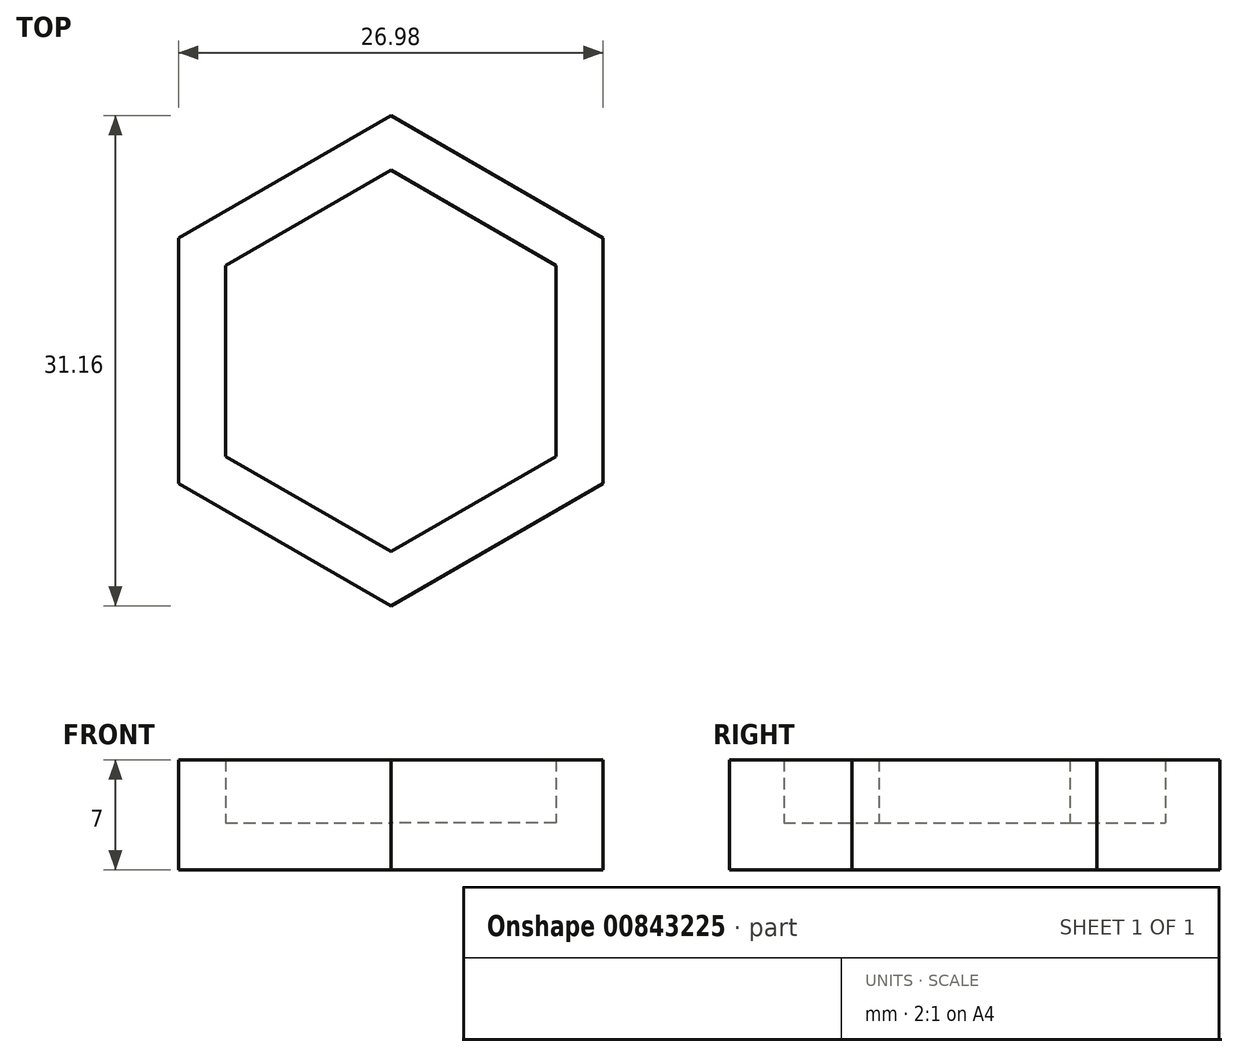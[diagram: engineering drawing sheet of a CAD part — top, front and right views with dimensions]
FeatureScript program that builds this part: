
annotation { "Feature Type Name" : "Feature", "Feature Type Description" : "" }
export const myFeature = defineFeature(function(context is Context, id is Id, definition is map)
    precondition{}
    {
        {
            var Q0;
            Q0=qCreatedBy(makeId("Top.planeOp"),FACE);
            var sketch = newSketch(context, id + "F0", { "sketchPlane" : qUnion([Q0])});
            skCircle(sketch, "E0.cCircle", {"center": v(0, 0) * mm, "radius": 10.49 * mm, "construction": true});
            skLineSegment(sketch, "E0.0", {"start": v(10.49, 6.06) * mm, "end": v(10.49, -6.06) * mm});
            skLineSegment(sketch, "E0.1", {"start": v(10.49, -6.06) * mm, "end": v(0, -12.11) * mm});
            skLineSegment(sketch, "E0.2", {"start": v(0, -12.11) * mm, "end": v(-10.49, -6.06) * mm});
            skLineSegment(sketch, "E0.3", {"start": v(-10.49, -6.06) * mm, "end": v(-10.5, 6.06) * mm});
            skLineSegment(sketch, "E0.4", {"start": v(-10.5, 6.06) * mm, "end": v(0, 12.11) * mm});
            skLineSegment(sketch, "E0.5", {"start": v(0, 12.11) * mm, "end": v(10.49, 6.06) * mm});
            skPoint(sketch, "E0.0.midPoint", {"position": v(10.49, 0) * mm});
            skLineSegment(sketch, "E1.0", {"start": v(-13.49, -7.79) * mm, "end": v(-13.49, 7.79) * mm});
            skLineSegment(sketch, "E1.1", {"start": v(0, 15.58) * mm, "end": v(13.49, 7.79) * mm});
            skLineSegment(sketch, "E1.2", {"start": v(13.49, 7.79) * mm, "end": v(13.49, -7.79) * mm});
            skLineSegment(sketch, "E1.3", {"start": v(-13.49, 7.79) * mm, "end": v(0, 15.58) * mm});
            skLineSegment(sketch, "E1.4", {"start": v(13.49, -7.79) * mm, "end": v(0, -15.58) * mm});
            skLineSegment(sketch, "E1.5", {"start": v(0, -15.58) * mm, "end": v(-13.49, -7.79) * mm});
            skSolve(sketch);
        }
        {
            var Q0;
            Q0 = qSketchRegion(id + "F0", true);
            var Q1;
            Q1=makeQuery(id+"F0.imprint","IMPRINT",FACE,{"disambiguationData":[TD([[makeQuery(id+"F0.imprint","IMPRINT",EDGE,{"derivedFrom":sQuery(id+"F0.wireOp",EDGE,"E0.0")}),-1.0]])]});
            extrude(context, id + "F1", {"entities" : qUnion([Q0, Q1]), "depth" : 3 * mm, "offsetDistance" : 25.4 * mm});
        }
        {
            var Q0;
            Q0=makeQuery(id+"F0.imprint","IMPRINT",FACE,{"disambiguationData":[TD([[makeQuery(id+"F0.imprint","IMPRINT",EDGE,{"derivedFrom":sQuery(id+"F0.wireOp",EDGE,"E0.0")}),1.0]])]});
            extrude(context, id + "F2", {"entities" : qUnion([Q0]), "operationType" : NewBodyOperationType.ADD, "depth" : 7 * mm, "offsetDistance" : 25.4 * mm});
        }
    });
